# Revit family: spectral_sinus_sinus_700_830_o-da_2180
name_source: partatom
category: Lighting Fixtures
revit_build: Autodesk Revit 2016 (Build: 20150220_1215(x64)
units: mm (PartAtom-declared; Revit-internal decimal feet)

## family parameters
Cut with Voids When Loaded = No
Host = Face
Light Source = No
Part Type = Normal
Room Calculation Point = No
Round Connector Dimension = Use Diameter
Shared = No

## types (1)
- SPECTRAL SINUS (1 x )
    Apparent Load = 0 VA
    Approval mark = CE
    CIE Flux Codes = 49 80 96 60 101
    Control Gear = Electronic transformer
    Default Elevation = 1800 mm
    Description = SPG0630001
LED pendant luminaire SINUS

Design:
LED pendant luminaire direct / indirect beam, single luminaire. Five very narrow sinusoidally curved luminaire bodies in a U-shape, cross-section 
40 x 40 mm, made of extruded aluminium, arranged alternately in parallel, linked by round tubular profiles made of extruded aluminium. Three luminaire bodies for the direct and two for the indirect lighting component. Colour outside structured white similar to RAL9016, black similar to RAL9005 (…-AQ) or silver similar to RAL9006 (…-SI), inside high-reflectance white powder coated. Flexible LED modules mounted in the luminaire body. Direct and indirect lighting component emitted through a opal plastic cover made of 
UV-stabilized PMMA, separately switchable and dimmable. Canopy in extruded aluminium, cross-section 60 x 60 mm, for ceiling mounting.

Electronic DALI converter for LED, 220-240 Volt, 0/50-60 Hz and internal connector block 5 x 2,5mm2, prefitted in separate canopy. Luminaire with transparent connecting cables suspended at the canopy for ceiling mounting.
    Height = 190 mm
    Lamp = 1 x
    Lamp count = 1
    Length = 1574 mm
    Luminous efficacy = 0 lm/W
    Manufacturer = Ridi
    ModVariant = No
    Model = SINUS 700/830 O-DA
    Mounting Place = Ceiling
    Mounting Type = Pendant
    Number of Poles = 1
    OnlyDefault = Yes
    Power Factor = 1
    Product Name = SPECTRAL SINUS
    Product group = Pendant luminaire
    ProductGroupID = 9
    Protection Class = Protection class
    Protection Degree = IP 20
    RlxData = <blob elided: 31553 chars, md5=e8c993e1>
    Socket = socket
    Standby Power = 0 W
    System Light Flux = 0 lm
    System Power = 0 W
    Type Image = sinus_quer_frei_klein.jpg
    URL = http://reluxnet.relux.com
    VarID = 1
    Voltage = 0 V
    Weight = 0.00 kg
    Width = 520 mm

## geometry (parser evidence)
native form markers: Blend x4, Sweep x15
no freeform markers — native parametric forms only
